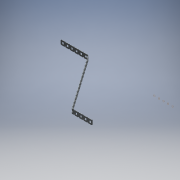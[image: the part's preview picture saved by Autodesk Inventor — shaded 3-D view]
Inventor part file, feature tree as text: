
AUTODESK INVENTOR PART (.ipt)
format: ipt  version: 2018 (Build 220112000, 112)  size: 660,480 bytes
history: native  units: mm (DEFAULTED — no unit token found)
features: other x26, extrude x25, sketch x4, sheet_metal_op x3, pattern_linear x2
ambient origin geometry x8: Origin, YZ Plane, XZ Plane, XY Plane, X Axis, Y Axis, Z Axis, Center Point
bodies: Solid1 (feature_tree)
feature tree (60):
  sheet_metal_op  "Face1"
  pattern_linear  "Rectangular Pattern1"  Spacing1=1.905mm  [1 undecoded]
  pattern_linear  "Rectangular Pattern2"  Spacing1=1.905mm  [1 undecoded]
  sheet_metal_op  "Fold1"
  sheet_metal_op  "Fold2"
  sketch  "Sketch1"  dims[d0=12.7mm]
  other  "Plate1"
  sketch  "Sketch4"  dims[d1=12.7mm]
  other  "Srf1"
  other  "Srf2"
  other  "Srf3"
  other  "Srf4"
  other  "Srf5"
  other  "Srf6"
  other  "Srf7"
  other  "Srf8"
  other  "Srf9"
  other  "Srf10"
  other  "Srf11"
  other  "Srf12"
  other  "Srf13"
  other  "Srf14"
  other  "Srf15"
  other  "Srf16"
  other  "Srf17"
  other  "Srf18"
  other  "Srf19"
  other  "Srf20"
  other  "Srf21"
  other  "Srf22"
  other  "Srf23"
  other  "Srf24"
  other  "Srf25"
  sketch  "Sketch5"  dims[d2=1.905mm]
  sketch  "Sketch6"  dims[d3=1.905mm d4=1.905mm d5=1.905mm d6=1.905mm d7=1.905mm d8=1.905mm d9=1.905mm d10=4.6228mm d11=4.6228mm d12=4.064mm d13=4.064mm d14=1.27mm d15=250.0mm d17=12.7mm d18=0.508mm d19=25.4mm d20=0.0mm d21=250.0mm d23=12.7mm d24=0.0mm d25=0.0mm d26=0.0mm d27=0.0mm d28=0.0mm d29=0.0mm d30=0.0mm d31=0.0mm d32=0.0mm d33=0.0mm d34=0.0mm d35=0.0mm d36=0.0mm d37=0.0mm d38=0.0mm d39=0.0mm d40=0.0mm d41=0.0mm d42=0.0mm d43=0.0mm d44=0.0mm d45=0.0mm d46=0.0mm d47=0.0mm d48=0.0mm d49=0.0mm d50=0.0mm d51=0.0mm d52=0.0mm d53=0.0mm d54=0.0mm d55=0.0mm d56=0.0mm d57=0.0mm d58=0.0mm d59=0.0mm d60=0.0mm d61=0.0mm d62=0.0mm d63=0.0mm d64=1.27mm d65=1.27mm d66=0.635mm d67=2.54mm d68=1.27mm d69=9.599311mm d70=1.27mm d71=1.27mm d72=0.635mm d73=2.54mm d74=1.27mm d75=9.599311mm d76=1.27mm]
  extrude  "ExtrusionSrf1"  Depth=1.27mm
  extrude  "ExtrusionSrf2"  Depth=1.27mm
  extrude  "ExtrusionSrf3"  Depth=1.27mm
  extrude  "ExtrusionSrf4"  Depth=1.27mm
  extrude  "ExtrusionSrf5"  Depth=4.6228mm
  extrude  "ExtrusionSrf6"  Depth=4.6228mm
  extrude  "ExtrusionSrf7"  Depth=4.064mm
  extrude  "ExtrusionSrf8"  Depth=4.064mm
  extrude  "ExtrusionSrf9"  Depth=1.27mm
  extrude  "ExtrusionSrf10"  Depth=12.7mm
  extrude  "ExtrusionSrf11"  Depth=0.508mm
  extrude  "ExtrusionSrf12"  Depth=1.27mm TaperAngle=0.0deg
  extrude  "ExtrusionSrf13"  Depth=12.7mm
  extrude  "ExtrusionSrf14"  Depth=1.27mm
  extrude  "ExtrusionSrf15"  Depth=1.27mm
  extrude  "ExtrusionSrf16"  Depth=1.27mm
  extrude  "ExtrusionSrf17"  Depth=2.54mm
  extrude  "ExtrusionSrf18"  Depth=1.27mm
  extrude  "ExtrusionSrf19"  Depth=1.27mm
  extrude  "ExtrusionSrf20"  Depth=1.27mm
  extrude  "ExtrusionSrf21"  Depth=1.27mm
  extrude  "ExtrusionSrf22"  Depth=2.54mm
  extrude  "ExtrusionSrf23"  Depth=1.27mm
  extrude  "ExtrusionSrf24"  Depth=1.27mm
  extrude  "ExtrusionSrf25"  [1 undecoded]
note: 3 required parameter values undecoded (feature->parameter linkage not recoverable at this tier; creation-order binding heuristic only, values carry confidence <= 0.55)
